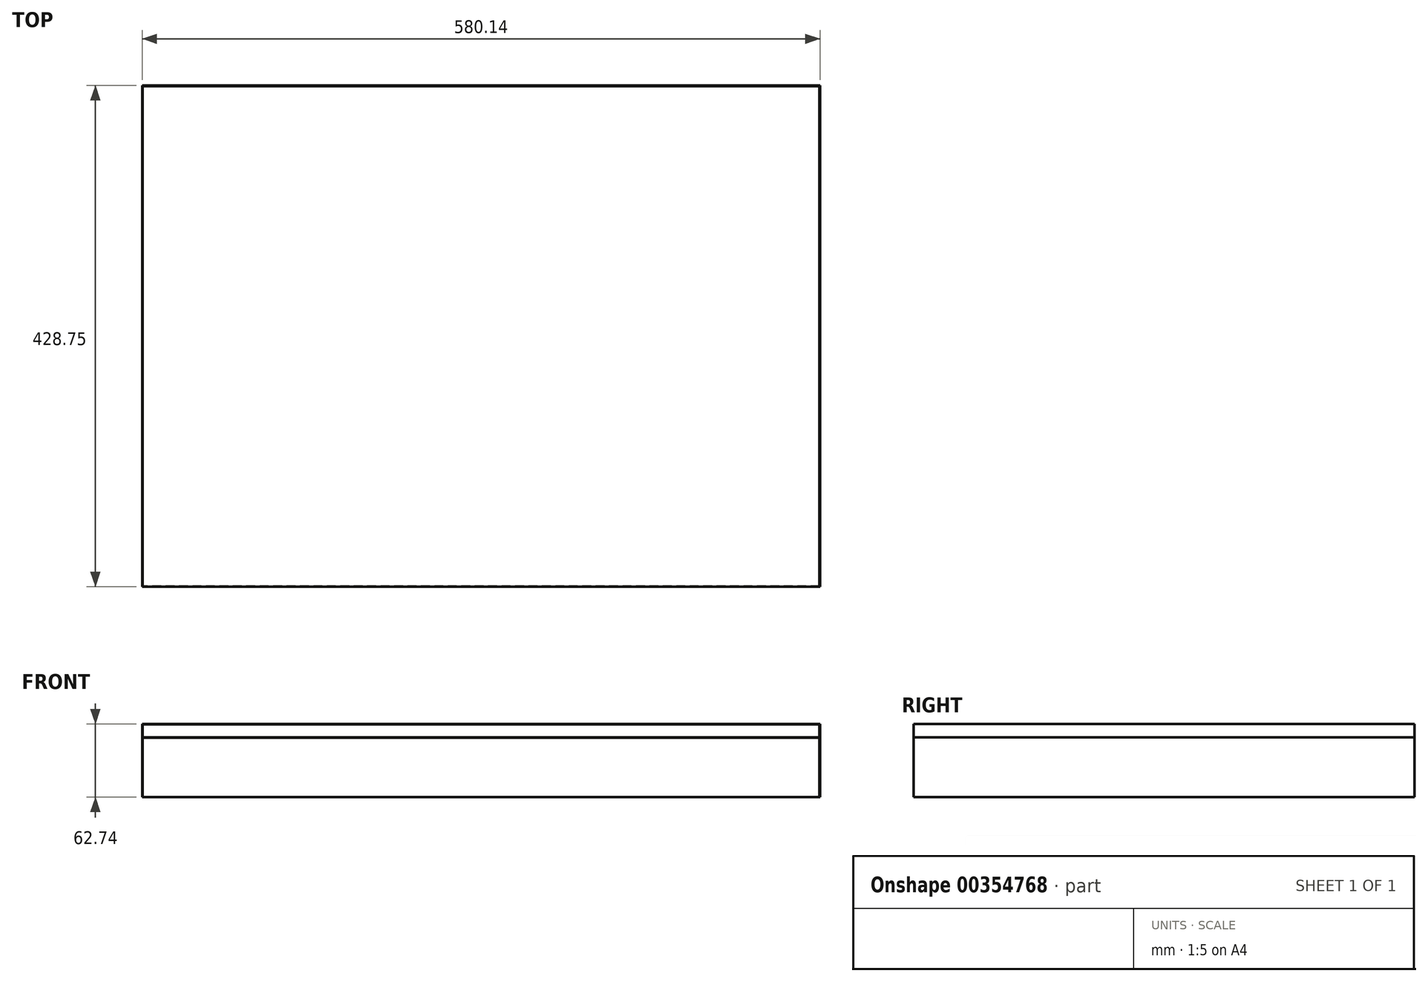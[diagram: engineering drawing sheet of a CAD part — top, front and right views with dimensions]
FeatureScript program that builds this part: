
annotation { "Feature Type Name" : "Feature", "Feature Type Description" : "" }
export const myFeature = defineFeature(function(context is Context, id is Id, definition is map)
    precondition{}
    {
        {
            assignVariable(context, id + "F0", {"name" : "Thk", "anyValue" : .47});
        }
        {
            var Q0;
            Q0=qCreatedBy(makeId("Top.planeOp"),FACE);
            var sketch = newSketch(context, id + "F1", { "sketchPlane" : qUnion([Q0])});
            skLineSegment(sketch, "E0.bottom", {"start": v(-290.07, 0) * mm, "end": v(290.07, 0) * mm});
            skLineSegment(sketch, "E0.top", {"start": v(-290.07, -428.75) * mm, "end": v(290.07, -428.75) * mm});
            skLineSegment(sketch, "E0.left", {"start": v(-290.07, 0) * mm, "end": v(-290.07, -428.75) * mm});
            skLineSegment(sketch, "E0.right", {"start": v(290.07, 0) * mm, "end": v(290.07, -428.75) * mm});
            skPoint(sketch, "E0.middle", {"position": v(0, -214.38) * mm});
            skSolve(sketch);
        }
        {
            var Q0;
            Q0=makeQuery(id+"F1.imprint","IMPRINT",FACE,{"disambiguationData":[TD([[makeQuery(id+"F1.imprint","IMPRINT",EDGE,{"derivedFrom":sQuery(id+"F1.wireOp",EDGE,"E0.bottom")}),-1.0]])]});
            extrude(context, id + "F2", {"entities" : qUnion([Q0]), "depth" : (getVariable(context, 'Thk')) * mm});
        }
        {
            var Q0;
            Q0=makeQuery(id+"F2.opExtrude","SWEPT_FACE",FACE,{"disambiguationData":[OSD([sQuery(id+"F1.wireOp",EDGE,"E0.top")])]});
            var sketch = newSketch(context, id + "F3", { "sketchPlane" : qUnion([Q0])});
            skLineSegment(sketch, "E1.bottom", {"start": v(-290.07, 11.94) * mm, "end": v(290.07, 11.94) * mm});
            skLineSegment(sketch, "E1.top", {"start": v(-290.07, -50.8) * mm, "end": v(290.07, -50.8) * mm});
            skLineSegment(sketch, "E1.left", {"start": v(-290.07, 11.94) * mm, "end": v(-290.07, -50.8) * mm});
            skLineSegment(sketch, "E1.right", {"start": v(290.07, 11.94) * mm, "end": v(290.07, -50.8) * mm});
            skSolve(sketch);
        }
        {
            var Q0;
            Q0=makeQuery(id+"F2.opExtrude","SWEPT_FACE",FACE,{"disambiguationData":[OSD([sQuery(id+"F1.wireOp",EDGE,"E0.left")])]});
            var sketch = newSketch(context, id + "F4", { "sketchPlane" : qUnion([Q0])});
            skLineSegment(sketch, "E2.bottom", {"start": v(428.75, 11.94) * mm, "end": v(0, 11.94) * mm});
            skLineSegment(sketch, "E2.top", {"start": v(428.75, -50.8) * mm, "end": v(0, -50.8) * mm});
            skLineSegment(sketch, "E2.left", {"start": v(428.75, 11.94) * mm, "end": v(428.75, -50.8) * mm});
            skLineSegment(sketch, "E2.right", {"start": v(0, 11.94) * mm, "end": v(0, -50.8) * mm});
            skSolve(sketch);
        }
        {
            var Q0;
            Q0 = qSketchRegion(id + "F4", true);
            extrude(context, id + "F5", {"entities" : qUnion([Q0]), "oppositeDirection" : true, "depth" : (getVariable(context, 'Thk')) * mm});
        }
        {
            var Q0;
            Q0=makeQuery(id+"F5.opExtrude","SWEPT_BODY",BODY,{"disambiguationData":[OSD([sQuery(id+"F4.wireOp",EDGE,"E2.bottom"),sQuery(id+"F4.wireOp",EDGE,"E2.top"),sQuery(id+"F4.wireOp",EDGE,"E2.left"),sQuery(id+"F4.wireOp",EDGE,"E2.right")])]});
            var Q1;
            Q1=qCreatedBy(makeId("Right.planeOp"),FACE);
            mirror(context, id + "F6", {"entities" : qUnion([Q0]), "mirrorPlane" : qUnion([Q1])});
        }
        {
            var Q0;
            Q0=makeQuery(id+"F6.opPattern","COPY",FACE,{"derivedFrom":makeQuery(id+"F5.opExtrude","SWEPT_FACE",FACE,{"disambiguationData":[OSD([sQuery(id+"F4.wireOp",EDGE,"E2.right")])]}),"instanceName":"1"});
            var sketch = newSketch(context, id + "F7", { "sketchPlane" : qUnion([Q0])});
            skLineSegment(sketch, "E3.bottom", {"start": v(-290.07, -50.8) * mm, "end": v(290.07, -50.8) * mm});
            skLineSegment(sketch, "E3.top", {"start": v(-290.07, 11.94) * mm, "end": v(290.07, 11.94) * mm});
            skLineSegment(sketch, "E3.left", {"start": v(-290.07, -50.8) * mm, "end": v(-290.07, 11.94) * mm});
            skLineSegment(sketch, "E3.right", {"start": v(290.07, -50.8) * mm, "end": v(290.07, 11.94) * mm});
            skSolve(sketch);
        }
        {
            var Q0;
            Q0 = qSketchRegion(id + "F7", true);
            extrude(context, id + "F8", {"entities" : qUnion([Q0]), "oppositeDirection" : true, "depth" : (getVariable(context, 'Thk')) * mm});
        }
        {
            var Q0;
            Q0=makeQuery(id+"F2.opExtrude","CAP_EDGE",EDGE,{"disambiguationData":[OSD([sQuery(id+"F1.wireOp",EDGE,"E0.top")])],"isStart":true});
            var Q1;
            Q1=makeQuery(id+"F2.opExtrude","CAP_EDGE",EDGE,{"disambiguationData":[OSD([sQuery(id+"F1.wireOp",EDGE,"E0.right")])],"isStart":true});
            var Q2;
            Q2=makeQuery(id+"F2.opExtrude","CAP_EDGE",EDGE,{"disambiguationData":[OSD([sQuery(id+"F1.wireOp",EDGE,"E0.left")])],"isStart":true});
            var Q3;
            Q3=makeQuery(id+"F2.opExtrude","CAP_EDGE",EDGE,{"disambiguationData":[OSD([sQuery(id+"F1.wireOp",EDGE,"E0.bottom")])],"isStart":true});
            chamfer(context, id + "F9", {"entities" : qUnion([Q0, Q1, Q2, Q3]), "width" : (getVariable(context, 'Thk')) * mm, "tangentPropagation" : true});
        }
        {
            var Q0;
            Q0=makeQuery(id+"FYY6Fko5XuCsR6T_2.opExtrude","CAP_EDGE",EDGE,{"disambiguationData":[OSD([sQuery(id+"F3.wireOp",EDGE,"E1.left")])],"isStart":false});
            var Q1;
            Q1=makeQuery(id+"F5.opExtrude","CAP_EDGE",EDGE,{"disambiguationData":[OSD([sQuery(id+"F4.wireOp",EDGE,"E2.left")])],"isStart":false});
            var Q2;
            Q2=makeQuery(id+"FYY6Fko5XuCsR6T_2.opExtrude","CAP_EDGE",EDGE,{"disambiguationData":[OSD([sQuery(id+"F3.wireOp",EDGE,"E1.right")])],"isStart":false});
            var Q3;
            Q3=makeQuery(id+"F6.opPattern","COPY",EDGE,{"derivedFrom":makeQuery(id+"F5.opExtrude","CAP_EDGE",EDGE,{"disambiguationData":[OSD([sQuery(id+"F4.wireOp",EDGE,"E2.left")])],"isStart":false}),"instanceName":"1"});
            var Q4;
            Q4=makeQuery(id+"F6.opPattern","COPY",EDGE,{"derivedFrom":makeQuery(id+"F5.opExtrude","CAP_EDGE",EDGE,{"disambiguationData":[OSD([sQuery(id+"F4.wireOp",EDGE,"E2.bottom")])],"isStart":false}),"instanceName":"1"});
            var Q5;
            Q5=makeQuery(id+"FYY6Fko5XuCsR6T_2.opExtrude","CAP_EDGE",EDGE,{"disambiguationData":[OSD([sQuery(id+"F3.wireOp",EDGE,"E1.bottom")])],"isStart":false});
            var Q6;
            Q6=makeQuery(id+"F5.opExtrude","CAP_EDGE",EDGE,{"disambiguationData":[OSD([sQuery(id+"F4.wireOp",EDGE,"E2.bottom")])],"isStart":false});
            var Q7;
            Q7=makeQuery(id+"F8.opExtrude","CAP_EDGE",EDGE,{"disambiguationData":[OSD([sQuery(id+"F7.wireOp",EDGE,"E3.left")])],"isStart":false});
            var Q8;
            Q8=makeQuery(id+"F8.opExtrude","CAP_EDGE",EDGE,{"disambiguationData":[OSD([sQuery(id+"F7.wireOp",EDGE,"E3.right")])],"isStart":false});
            var Q9;
            Q9=makeQuery(id+"F6.opPattern","COPY",EDGE,{"derivedFrom":makeQuery(id+"F5.opExtrude","CAP_EDGE",EDGE,{"disambiguationData":[OSD([sQuery(id+"F4.wireOp",EDGE,"E2.right")])],"isStart":false}),"instanceName":"1"});
            var Q10;
            Q10=makeQuery(id+"F8.opExtrude","CAP_EDGE",EDGE,{"disambiguationData":[OSD([sQuery(id+"F7.wireOp",EDGE,"E3.top")])],"isStart":false});
            var Q11;
            Q11=makeQuery(id+"F5.opExtrude","CAP_EDGE",EDGE,{"disambiguationData":[OSD([sQuery(id+"F4.wireOp",EDGE,"E2.right")])],"isStart":false});
            chamfer(context, id + "F10", {"entities" : qUnion([Q0, Q1, Q2, Q3, Q4, Q5, Q6, Q7, Q8, Q9, Q10, Q11]), "width" : (getVariable(context, 'Thk')) * mm, "tangentPropagation" : true});
        }
    });
